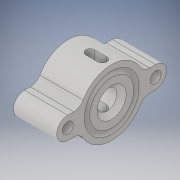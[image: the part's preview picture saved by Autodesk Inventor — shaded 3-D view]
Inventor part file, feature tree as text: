
AUTODESK INVENTOR PART (.ipt)
format: ipt  version: 2018 (Build 220112000, 112)  size: 336,896 bytes
history: native  units: in
note: dims shown in document units (in); Inventor stores cm internally (conversion verified against a paired STEP export)
features: sketch x8, projected_geometry x7, extrude x6, revolve x2, pattern_circular x2, fillet x1
ambient origin geometry x8: Origin, YZ Plane, XZ Plane, XY Plane, X Axis, Y Axis, Z Axis, Center Point
bodies: Body1 (feature_tree)
feature tree (26):
  sketch  "Sketch2"  dims[d10=0.75in d13=90.0deg]
  revolve  "Revolution1"  Angle=90.0deg
  revolve  "Revolution2"  [1 undecoded]
  extrude  "Extrusion4"  Depth=0.225in
  pattern_circular  "Circular Pattern2"  [2 undecoded]
  extrude  "Extrusion5"  Depth=0.125in
  extrude  "Extrusion6"  Depth=0.25in
  extrude  "Extrusion7"  Depth=0.1in
  sketch  "Sketch9"  dims[d41=0.5625in]
  extrude  "Extrusion8"  Depth=0.25in
  fillet  "Fillet3"  Radius=0.16in
  pattern_circular  "Circular Pattern3"  [2 undecoded]
  extrude  "Extrusion9"  Depth=0.25in TaperAngle=360.0deg
  sketch  "Sketch5"  dims[d35=45.0deg d36=0.02in]
  projected_geometry  "Projected Loop2"
  sketch  "Sketch6"  dims[d37=0.625in d38=0.225in]
  projected_geometry  "Projected Loop3"
  projected_geometry  "Projected Loop4"
  sketch  "Sketch7"  dims[d39=0.3325in]
  projected_geometry  "Projected Loop5"
  sketch  "Sketch8"  dims[d40=0.12in]
  projected_geometry  "Projected Loop6"
  projected_geometry  "Projected Loop7"
  sketch  "Sketch10"  dims[d42=90.0deg]
  sketch  "Sketch11"  dims[d43=0.0905in d44=0.825in d45=0.125in d46=0.375in d47=0.1in d48=0.0625in d49=0.16in d50=1.0in d51=0.0in d52=3.937in d53=360.0deg d55=1.0in d56=0.0in d57=0.25in d58=0.0in d59=0.15in d60=0.2in d61=0.0in d62=0.2in d63=0.0in d64=0.25in d65=0.7874in d66=360.0deg d69=0.25in d70=1.0in d71=0.0in]
  projected_geometry  "Projected Loop8"
note: 5 required parameter values undecoded (feature->parameter linkage not recoverable at this tier; creation-order binding heuristic only, values carry confidence <= 0.55)